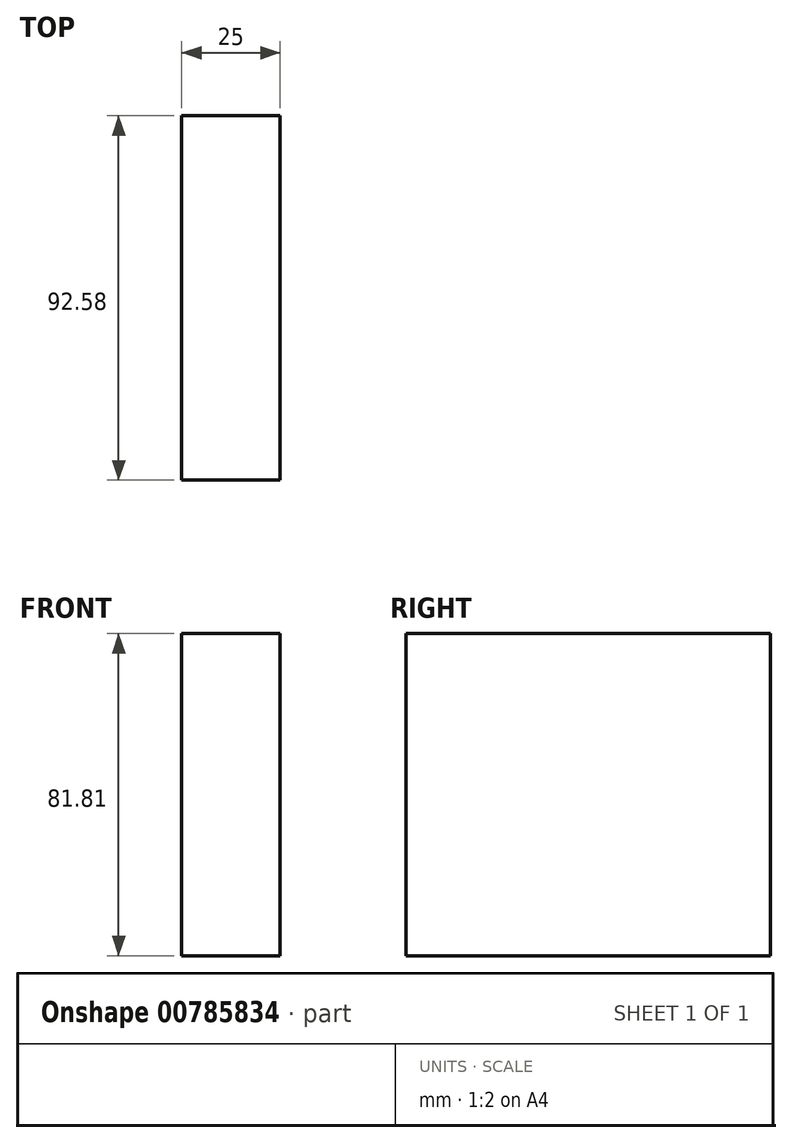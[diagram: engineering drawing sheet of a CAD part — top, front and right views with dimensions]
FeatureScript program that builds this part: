
annotation { "Feature Type Name" : "Feature", "Feature Type Description" : "" }
export const myFeature = defineFeature(function(context is Context, id is Id, definition is map)
    precondition{}
    {
        {
            var Q0;
            Q0=qCreatedBy(makeId("Right.planeOp"),FACE);
            var sketch = newSketch(context, id + "F0", { "sketchPlane" : qUnion([Q0])});
            skLineSegment(sketch, "E0", {"start": v(-44.35, 36.72) * mm, "end": v(48.23, 36.72) * mm});
            skLineSegment(sketch, "E1", {"start": v(48.23, 36.72) * mm, "end": v(48.23, -45.1) * mm});
            skLineSegment(sketch, "E2", {"start": v(48.23, -45.1) * mm, "end": v(-44.35, -45.1) * mm});
            skLineSegment(sketch, "E3", {"start": v(-44.35, -45.1) * mm, "end": v(-44.35, 36.72) * mm});
            skSolve(sketch);
        }
        {
            var Q0;
            Q0=makeQuery(id+"F0.imprint","IMPRINT",FACE,{"disambiguationData":[TD([[makeQuery(id+"F0.imprint","IMPRINT",EDGE,{"derivedFrom":sQuery(id+"F0.wireOp",EDGE,"E0")}),-1.0]])]});
            extrude(context, id + "F1", {"entities" : qUnion([Q0]), "depth" : 25 * mm, "offsetDistance" : 25 * mm});
        }
    });
